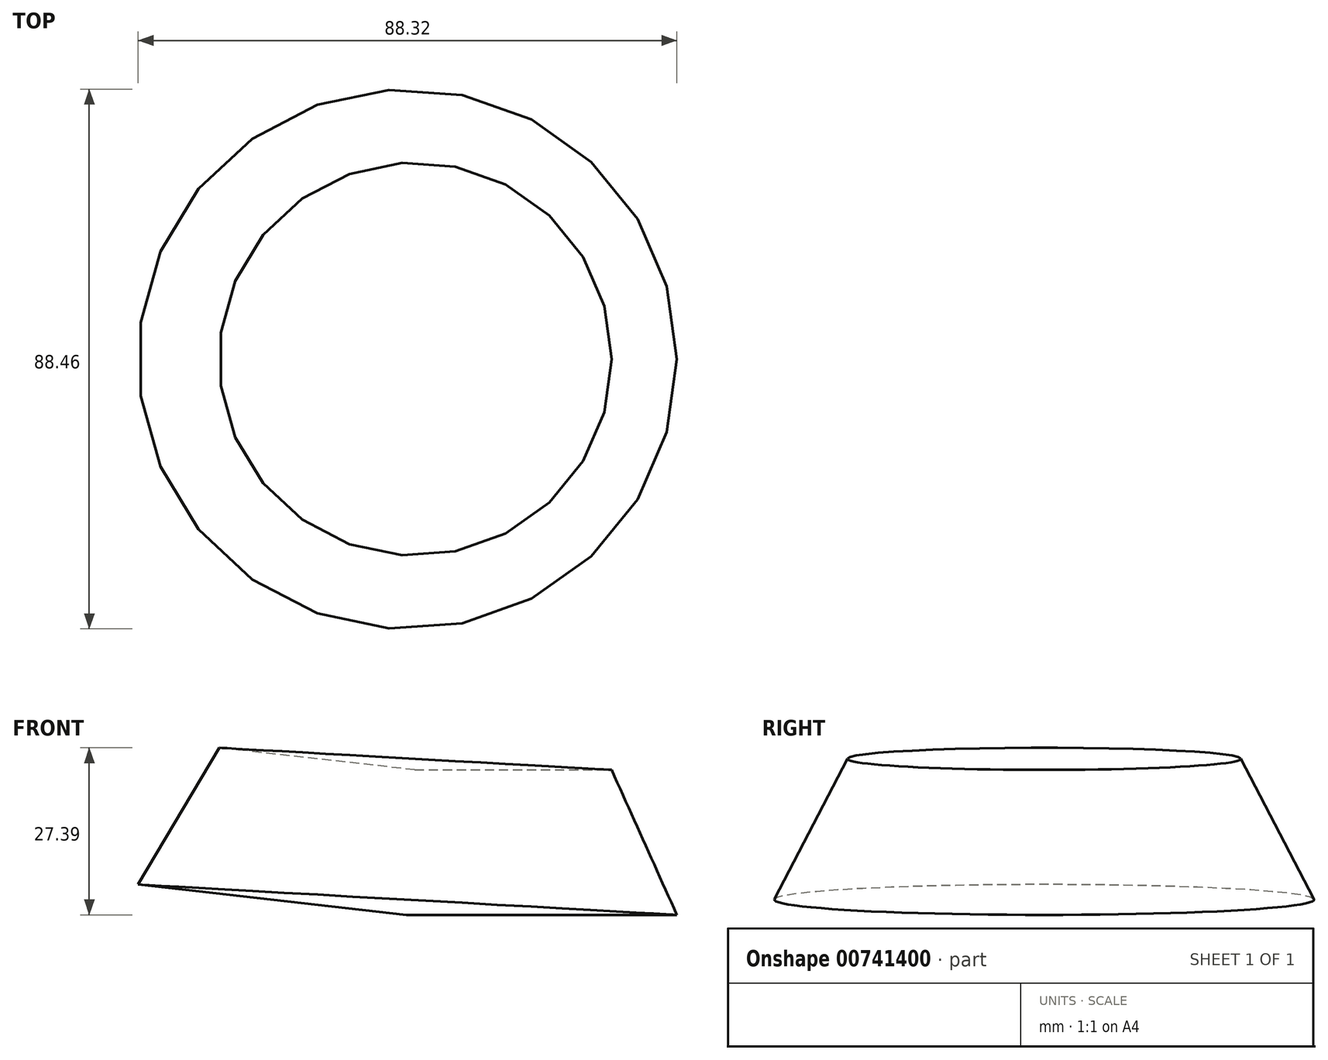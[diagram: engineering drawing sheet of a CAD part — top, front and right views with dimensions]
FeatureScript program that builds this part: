
annotation { "Feature Type Name" : "Feature", "Feature Type Description" : "" }
export const myFeature = defineFeature(function(context is Context, id is Id, definition is map)
    precondition{}
    {
        {
            var Q0;
            Q0=qCreatedBy(makeId("Front.planeOp"),FACE);
            var sketch = newSketch(context, id + "F0", { "sketchPlane" : qUnion([Q0])});
            skLineSegment(sketch, "E0", {"start": v(-17.47, 0) * mm, "end": v(26.83, 0) * mm});
            skLineSegment(sketch, "E1", {"start": v(26.83, 0) * mm, "end": v(16.14, 23.77) * mm});
            skLineSegment(sketch, "E2", {"start": v(16.14, 23.77) * mm, "end": v(-16.14, 23.77) * mm});
            skLineSegment(sketch, "E3", {"start": v(-16.14, 23.77) * mm, "end": v(-17.47, 0) * mm});
            skSolve(sketch);
        }
        {
            var Q0;
            Q0=makeQuery(id+"F0.imprint","IMPRINT",FACE,{"disambiguationData":[TD([[makeQuery(id+"F0.imprint","IMPRINT",EDGE,{"derivedFrom":sQuery(id+"F0.wireOp",EDGE,"E0")}),1.0]])]});
            var Q1;
            Q1=sQuery(id+"F0.wireOp",EDGE,"E3");
            revolve(context, id + "F1", {"surfaceOperationType" : NewSurfaceOperationType.NEW, "entities" : qUnion([Q0]), "axis" : qUnion([Q1]), "revolveType" : RevolveType.FULL});
        }
    });
